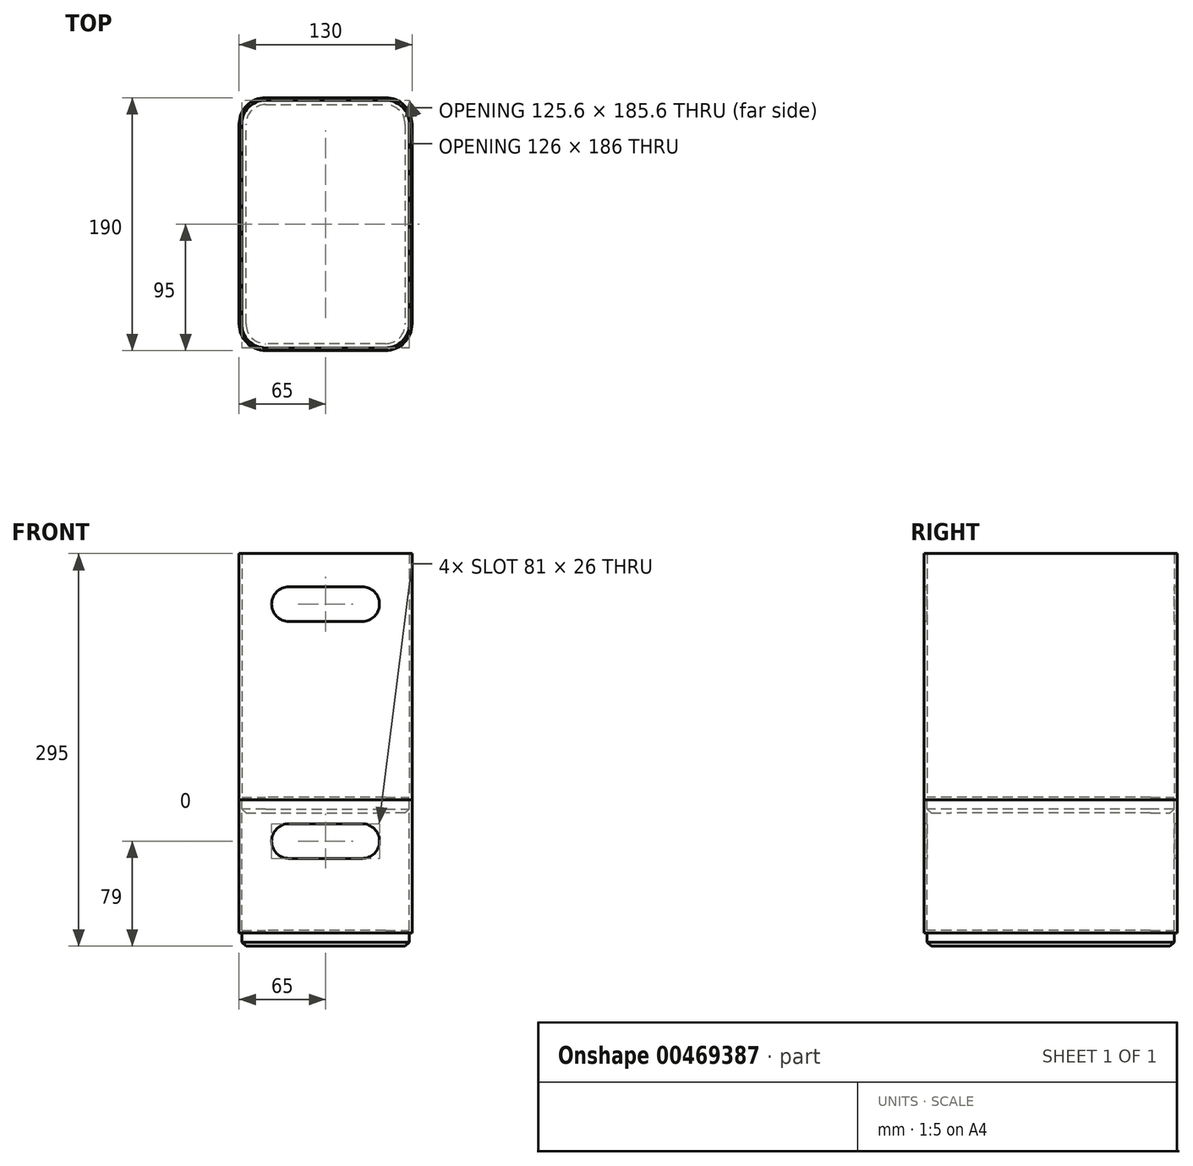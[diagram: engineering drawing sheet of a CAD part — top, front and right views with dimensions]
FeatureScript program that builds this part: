
annotation { "Feature Type Name" : "Feature", "Feature Type Description" : "" }
export const myFeature = defineFeature(function(context is Context, id is Id, definition is map)
    precondition{}
    {
        {
            assignVariable(context, id + "F0", {"name" : "t_wall", "anyValue" : 2});
        }
        {
            var Q0;
            Q0=qCreatedBy(makeId("Top.planeOp"),FACE);
            var sketch = newSketch(context, id + "F1", { "sketchPlane" : qUnion([Q0])});
            skLineSegment(sketch, "E0.bottom", {"start": v(45, 95) * mm, "end": v(-45, 95) * mm});
            skLineSegment(sketch, "E0.top", {"start": v(45, -95) * mm, "end": v(-45, -95) * mm});
            skLineSegment(sketch, "E0.left", {"start": v(65, 75) * mm, "end": v(65, -75) * mm});
            skLineSegment(sketch, "E0.right", {"start": v(-65, 75) * mm, "end": v(-65, -75) * mm});
            skPoint(sketch, "E0.middle", {"position": v(0, 0) * mm});
            skPoint(sketch, "E1.visualSharp", {"position": v(-65, 95) * mm});
            skArc(sketch, "E1.filletArc", {"start": v(-45, 95) * mm, "mid": v(-59.14, 89.14) * mm, "end": v(-65, 75) * mm});
            skPoint(sketch, "E2.visualSharp", {"position": v(-65, -95) * mm});
            skArc(sketch, "E2.filletArc", {"start": v(-65, -75) * mm, "mid": v(-59.14, -89.14) * mm, "end": v(-45, -95) * mm});
            skPoint(sketch, "E3.visualSharp", {"position": v(65, -95) * mm});
            skArc(sketch, "E3.filletArc", {"start": v(45, -95) * mm, "mid": v(59.14, -89.14) * mm, "end": v(65, -75) * mm});
            skPoint(sketch, "E4.visualSharp", {"position": v(65, 95) * mm});
            skArc(sketch, "E4.filletArc", {"start": v(65, 75) * mm, "mid": v(59.14, 89.14) * mm, "end": v(45, 95) * mm});
            skLineSegment(sketch, "E5.0", {"start": v(-62.8, 75) * mm, "end": v(-62.8, -75) * mm});
            skArc(sketch, "E5.1", {"start": v(-45, 92.8) * mm, "mid": v(-57.59, 87.59) * mm, "end": v(-62.8, 75) * mm});
            skArc(sketch, "E5.2", {"start": v(-62.8, -75) * mm, "mid": v(-57.59, -87.59) * mm, "end": v(-45, -92.8) * mm});
            skLineSegment(sketch, "E5.3", {"start": v(45, 92.8) * mm, "end": v(-45, 92.8) * mm});
            skLineSegment(sketch, "E5.4", {"start": v(45, -92.8) * mm, "end": v(-45, -92.8) * mm});
            skArc(sketch, "E5.5", {"start": v(45, -92.8) * mm, "mid": v(57.59, -87.59) * mm, "end": v(62.8, -75) * mm});
            skLineSegment(sketch, "E5.6", {"start": v(62.8, 75) * mm, "end": v(62.8, -75) * mm});
            skArc(sketch, "E5.7", {"start": v(62.8, 75) * mm, "mid": v(57.59, 87.59) * mm, "end": v(45, 92.8) * mm});
            skSolve(sketch);
        }
        {
            var Q0;
            Q0=makeQuery(id+"F1.imprint","IMPRINT",FACE,{"disambiguationData":[TD([[makeQuery(id+"F1.imprint","IMPRINT",EDGE,{"derivedFrom":sQuery(id+"F1.wireOp",EDGE,"E5.0")}),1.0]])]});
            var Q1;
            Q1=makeQuery(id+"F1.imprint","IMPRINT",FACE,{"disambiguationData":[TD([[makeQuery(id+"F1.imprint","IMPRINT",EDGE,{"derivedFrom":sQuery(id+"F1.wireOp",EDGE,"E0.bottom")}),1.0]])]});
            extrude(context, id + "F2", {"entities" : qUnion([Q0, Q1]), "depth" : 185 * mm, "offsetDistance" : 25 * mm});
        }
        {
            var Q0;
            Q0=makeQuery(id+"F2.opExtrude","CAP_FACE",FACE,{"disambiguationData":[OSD([sQuery(id+"F1.wireOp",EDGE,"E0.bottom"),sQuery(id+"F1.wireOp",EDGE,"E0.top"),sQuery(id+"F1.wireOp",EDGE,"E0.left"),sQuery(id+"F1.wireOp",EDGE,"E0.right"),sQuery(id+"F1.wireOp",EDGE,"E1.filletArc"),sQuery(id+"F1.wireOp",EDGE,"E2.filletArc"),sQuery(id+"F1.wireOp",EDGE,"E3.filletArc"),sQuery(id+"F1.wireOp",EDGE,"E4.filletArc")])],"isStart":false});
            shell(context, id + "F3", {"entities" : qUnion([Q0]), "thickness" : (getVariable(context, 't_wall')) * mm});
        }
        {
            var Q0;
            Q0=makeQuery(id+"F1.imprint","IMPRINT",FACE,{"disambiguationData":[TD([[makeQuery(id+"F1.imprint","IMPRINT",EDGE,{"derivedFrom":sQuery(id+"F1.wireOp",EDGE,"E5.0")}),1.0]])]});
            extrude(context, id + "F4", {"entities" : qUnion([Q0]), "operationType" : NewBodyOperationType.ADD, "oppositeDirection" : true, "depth" : 10 * mm, "offsetDistance" : 25 * mm});
        }
        {
            var Q0;
            Q0=makeQuery(id+"F1.imprint","IMPRINT",FACE,{"disambiguationData":[TD([[makeQuery(id+"F1.imprint","IMPRINT",EDGE,{"derivedFrom":sQuery(id+"F1.wireOp",EDGE,"E0.bottom")}),1.0]])]});
            var Q1;
            Q1=makeQuery(id+"F1.imprint","IMPRINT",FACE,{"disambiguationData":[TD([[makeQuery(id+"F1.imprint","IMPRINT",EDGE,{"derivedFrom":sQuery(id+"F1.wireOp",EDGE,"E5.0")}),1.0]])]});
            extrude(context, id + "F5", {"entities" : qUnion([Q0, Q1]), "oppositeDirection" : true, "depth" : 100 * mm, "offsetDistance" : 25 * mm});
        }
        {
            var Q0;
            Q0=makeQuery(id+"F5.opExtrude","CAP_FACE",FACE,{"disambiguationData":[OSD([sQuery(id+"F1.wireOp",EDGE,"E0.bottom"),sQuery(id+"F1.wireOp",EDGE,"E0.top"),sQuery(id+"F1.wireOp",EDGE,"E0.left"),sQuery(id+"F1.wireOp",EDGE,"E0.right"),sQuery(id+"F1.wireOp",EDGE,"E1.filletArc"),sQuery(id+"F1.wireOp",EDGE,"E2.filletArc"),sQuery(id+"F1.wireOp",EDGE,"E3.filletArc"),sQuery(id+"F1.wireOp",EDGE,"E4.filletArc")])],"isStart":true});
            shell(context, id + "F6", {"entities" : qUnion([Q0]), "thickness" : (getVariable(context, 't_wall')) * mm});
        }
        {
            var Q0;
            Q0=makeQuery(id+"F5.opExtrude","CAP_FACE",FACE,{"disambiguationData":[OSD([sQuery(id+"F1.wireOp",EDGE,"E0.bottom"),sQuery(id+"F1.wireOp",EDGE,"E0.top"),sQuery(id+"F1.wireOp",EDGE,"E0.left"),sQuery(id+"F1.wireOp",EDGE,"E0.right"),sQuery(id+"F1.wireOp",EDGE,"E1.filletArc"),sQuery(id+"F1.wireOp",EDGE,"E2.filletArc"),sQuery(id+"F1.wireOp",EDGE,"E3.filletArc"),sQuery(id+"F1.wireOp",EDGE,"E4.filletArc")])],"isStart":false});
            var sketch = newSketch(context, id + "F7", { "sketchPlane" : qUnion([Q0])});
            skLineSegment(sketch, "E6.0.0", {"start": v(62.8, 75) * mm, "end": v(62.8, -75) * mm});
            skArc(sketch, "E6.0.1", {"start": v(62.8, -75) * mm, "mid": v(57.59, -87.59) * mm, "end": v(45, -92.8) * mm});
            skLineSegment(sketch, "E6.0.2", {"start": v(45, -92.8) * mm, "end": v(-45, -92.8) * mm});
            skArc(sketch, "E6.0.3", {"start": v(-45, -92.8) * mm, "mid": v(-57.59, -87.59) * mm, "end": v(-62.8, -75) * mm});
            skLineSegment(sketch, "E6.0.4", {"start": v(-62.8, -75) * mm, "end": v(-62.8, 75) * mm});
            skArc(sketch, "E6.0.5", {"start": v(-62.8, 75) * mm, "mid": v(-57.59, 87.59) * mm, "end": v(-45, 92.8) * mm});
            skLineSegment(sketch, "E6.0.6", {"start": v(-45, 92.8) * mm, "end": v(45, 92.8) * mm});
            skArc(sketch, "E6.0.7", {"start": v(45, 92.8) * mm, "mid": v(57.59, 87.59) * mm, "end": v(62.8, 75) * mm});
            skSolve(sketch);
        }
        {
            var Q0;
            Q0 = qSketchRegion(id + "F7", true);
            extrude(context, id + "F8", {"entities" : qUnion([Q0]), "operationType" : NewBodyOperationType.ADD, "depth" : 10 * mm, "offsetDistance" : 25 * mm});
        }
        {
            var Q0;
            Q0=makeQuery(id+"F8.opExtrude","CAP_FACE",FACE,{"disambiguationData":[OSD([sQuery(id+"F7.wireOp",EDGE,"E6.0.0"),sQuery(id+"F7.wireOp",EDGE,"E6.0.1"),sQuery(id+"F7.wireOp",EDGE,"E6.0.2"),sQuery(id+"F7.wireOp",EDGE,"E6.0.3"),sQuery(id+"F7.wireOp",EDGE,"E6.0.4"),sQuery(id+"F7.wireOp",EDGE,"E6.0.5"),sQuery(id+"F7.wireOp",EDGE,"E6.0.6"),sQuery(id+"F7.wireOp",EDGE,"E6.0.7")])],"isStart":false});
            var Q1;
            Q1=makeQuery(id+"F4.opExtrude","CAP_FACE",FACE,{"disambiguationData":[OSD([sQuery(id+"F1.wireOp",EDGE,"E5.0"),sQuery(id+"F1.wireOp",EDGE,"E5.1"),sQuery(id+"F1.wireOp",EDGE,"E5.2"),sQuery(id+"F1.wireOp",EDGE,"E5.3"),sQuery(id+"F1.wireOp",EDGE,"E5.4"),sQuery(id+"F1.wireOp",EDGE,"E5.5"),sQuery(id+"F1.wireOp",EDGE,"E5.6"),sQuery(id+"F1.wireOp",EDGE,"E5.7")])],"isStart":false});
            chamfer(context, id + "F9", {"entities" : qUnion([Q0, Q1]), "width" : 3 * mm, "tangentPropagation" : true});
        }
        {
            var Q0;
            Q0=makeQuery(id+"F2.opExtrude","SWEPT_FACE",FACE,{"disambiguationData":[OSD([sQuery(id+"F1.wireOp",EDGE,"E0.top")])]});
            var sketch = newSketch(context, id + "F10", { "sketchPlane" : qUnion([Q0])});
            skLineSegment(sketch, "E7", {"start": v(0, 185) * mm, "end": v(0, 66.65) * mm, "construction": true});
            skPoint(sketch, "E7.endSnap0", {"position": v(0, 185) * mm});
            skLineSegment(sketch, "E8.bottom", {"start": v(27.5, 160) * mm, "end": v(-27.5, 160) * mm});
            skLineSegment(sketch, "E8.top", {"start": v(27.5, 134) * mm, "end": v(-27.5, 134) * mm});
            skLineSegment(sketch, "E8.left", {"start": v(27.5, 160) * mm, "end": v(27.5, 134) * mm});
            skLineSegment(sketch, "E8.right", {"start": v(-27.5, 160) * mm, "end": v(-27.5, 134) * mm});
            skPoint(sketch, "E8.middle", {"position": v(0, 147) * mm});
            skArc(sketch, "E9", {"start": v(-27.5, 160) * mm, "mid": v(-40.5, 147) * mm, "end": v(-27.5, 134) * mm});
            skArc(sketch, "E10", {"start": v(27.5, 134) * mm, "mid": v(40.5, 147) * mm, "end": v(27.5, 160) * mm});
            skLineSegment(sketch, "E11.0.1.0", {"start": v(27.5, -18) * mm, "end": v(-27.5, -18) * mm});
            skLineSegment(sketch, "E11.0.1.1", {"start": v(27.5, -44) * mm, "end": v(-27.5, -44) * mm});
            skArc(sketch, "E11.0.1.2", {"start": v(27.5, -44) * mm, "mid": v(40.5, -31) * mm, "end": v(27.5, -18) * mm});
            skLineSegment(sketch, "E11.0.1.3", {"start": v(27.5, -18) * mm, "end": v(27.5, -44) * mm});
            skArc(sketch, "E11.0.1.4", {"start": v(-27.5, -18) * mm, "mid": v(-40.5, -31) * mm, "end": v(-27.5, -44) * mm});
            skLineSegment(sketch, "E11.0.1.5", {"start": v(-27.5, -18) * mm, "end": v(-27.5, -44) * mm});
            skPoint(sketch, "E11.0.1.6", {"position": v(0, -31) * mm});
            skLineSegment(sketch, "E11.direction1", {"start": v(-27.5, 134) * mm, "end": v(-2.5, 134) * mm, "construction": true});
            skLineSegment(sketch, "E11.direction2", {"start": v(-27.5, 134) * mm, "end": v(-27.5, -44) * mm, "construction": true});
            skSolve(sketch);
        }
        {
            var Q0;
            Q0 = qSketchRegion(id + "F10", true);
            extrude(context, id + "F11", {"entities" : qUnion([Q0]), "operationType" : NewBodyOperationType.REMOVE, "endBound" : BoundingType.THROUGH_ALL, "oppositeDirection" : true, "depth" : 25 * mm, "offsetDistance" : 25 * mm});
        }
    });
